# Revit family: Verano_V908_Ledro_GM_R21
name_source: partatom
category: Generic Models
units: mm (PartAtom-declared; Revit-internal decimal feet)

## family parameters
Always vertical = Yes
Can host rebar = No
Cut with Voids When Loaded = No
Part Type = Normal
Room Calculation Point = No
Round Connector Dimension = Use Diameter
Shared = No
Work Plane-Based = No

## types (2) — shared parameters
Achtung = Keine Garantie auf Wasserdichtigkeit bei einem Gefälle von weniger als 7º
Attention = Water resistance is not guaranteed on slopes less than 7º
Manufacturer = Verano Systems
Max Angle = 15.00°
Max H1 = 6165 mm
Max Pillar Height = 5000 mm  [stored 16.4042 ft]
Maximal Projection = 4500 mm
Maximal Width = 14000 mm  [stored 45.9318 ft]
Min Angle = 5.00°
Minimal Projection = 2000 mm  [stored 6.56168 ft]
Minimal Width = 3000 mm  [stored 9.84252 ft]
Model = Ledro V908
URL = https://verano.nl
zero-valued in all types: Default Elevation

## per-type parameters (varying)
| type | Rounded | Straight |
| T1 - Rounded Profile | Yes | No |
| T2 - Straight Profile | No | Yes |

note: [stored X ft] marks values corroborated as IEEE doubles in the binary element streams (Revit-internal decimal feet)

## geometry (parser evidence)
native form markers: Extrusion x2, Sweep x38
no freeform markers — native parametric forms only
